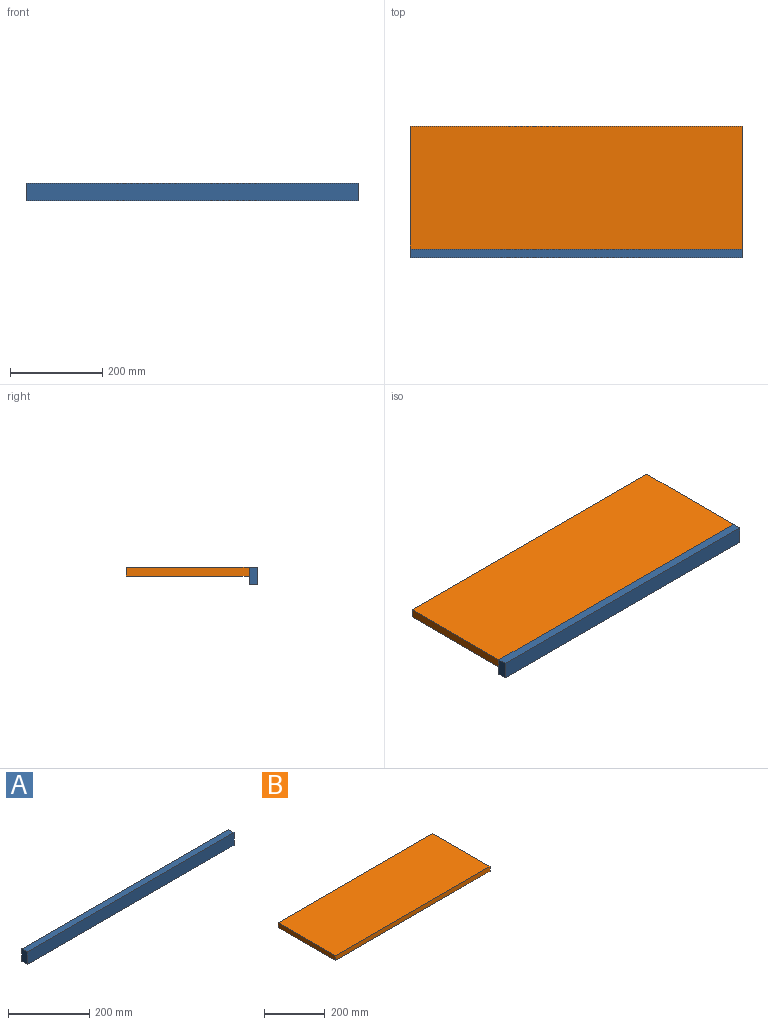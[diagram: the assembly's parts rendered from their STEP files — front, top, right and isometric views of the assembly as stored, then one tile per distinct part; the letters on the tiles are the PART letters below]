
ASSEMBLY  parts=2 mates=1
PART A: 6 faces, bbox 720.7x19.1x38.1 mm
  f0: plane 720.73x19.05mm, normal (0,0,1), area 13729.8mm2, adj f1,f3,f4,f5
  f1: plane 38.1x19.05mm, normal (-1,0,0), area 725.8mm2, adj f0,f2,f4,f5
  f2: plane 720.73x19.05mm, normal (0,0,-1), area 13729.8mm2, adj f1,f3,f4,f5
  f3: plane 38.1x19.05mm, normal (1,0,0), area 725.8mm2, adj f0,f2,f4,f5
  f4: plane 720.73x38.1mm, normal (0,-1,0), area 27459.6mm2, adj f0,f1,f2,f3
  f5: plane 720.73x38.1mm, normal (0,1,0), area 27459.6mm2, adj f0,f1,f2,f3
PART B: 6 faces, bbox 720.7x266.7x19.1 mm
  f0: plane 266.7x19.05mm, normal (-1,0,0), area 5080.6mm2, adj f1,f3,f4,f5
  f1: plane 720.73x266.7mm, normal (0,0,-1), area 192217.4mm2, adj f0,f2,f4,f5
  f2: plane 266.7x19.05mm, normal (1,0,0), area 5080.6mm2, adj f1,f3,f4,f5
  f3: plane 720.73x266.7mm, normal (0,0,1), area 192217.4mm2, adj f0,f2,f4,f5
  f4: plane 720.73x19.05mm, normal (0,-1,0), area 13729.8mm2, adj f0,f1,f2,f3
  f5: plane 720.73x19.05mm, normal (0,1,0), area 13729.8mm2, adj f0,f1,f2,f3
PLACE A t=(1109.66,0,-488.95)mm
PLACE B t=(1109.66,266.7,-127)mm
MATE fastened B.f4 <-> A.f5  axis (0,-1,0) through (0,0,19.05)mm
